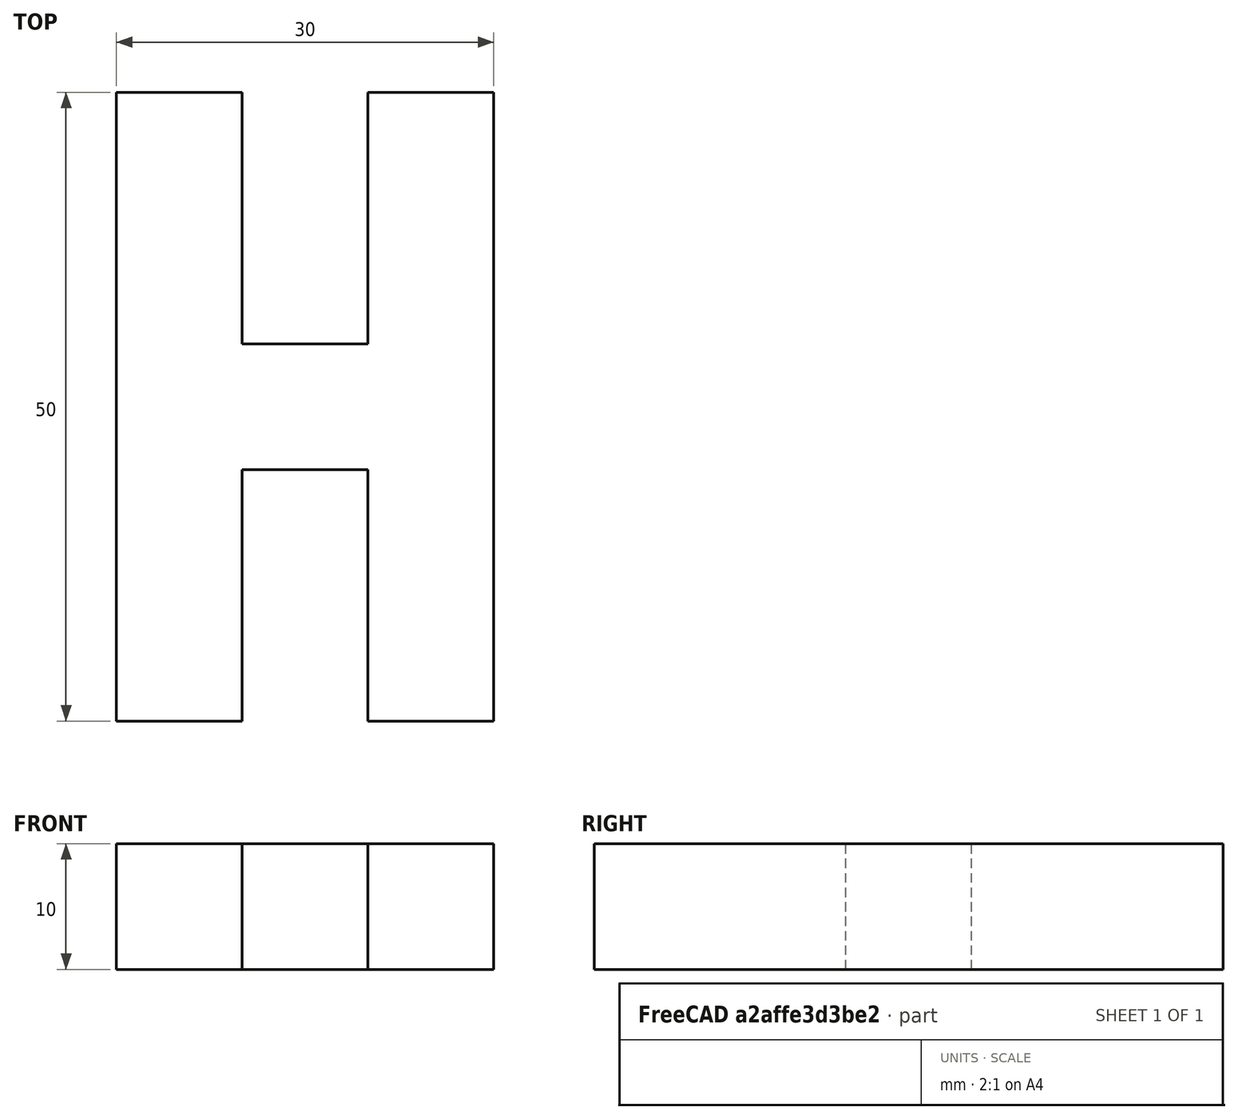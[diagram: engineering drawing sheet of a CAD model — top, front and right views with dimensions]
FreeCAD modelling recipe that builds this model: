
FCSTD DOCUMENT  (FreeCAD 0.21R33694 (Git))
Label: OJT1_T18R02_hola
License: All rights reserved
LicenseURL: https://en.wikipedia.org/wiki/All_rights_reserved
objects: Sketcher::SketchObject×2, PartDesign::Pad×1, PartDesign::Body×1
note: 5 computed .brp shape members not serialized (recipe doc carries the construction recipe); baked Part::Feature solids carry a one-line shape summary decoded from their .brp

FEATURE [Sketcher::SketchObject] Sketch
  FullyConstrained = false
  MapMode = 5
  Support = -> [XY_Plane]
  sketch-geometry (12):
    g0: LineSegment StartX=17.5793 StartY=23.0862 StartZ=0 EndX=17.5793 EndY=-26.9138 EndZ=0
    g1: LineSegment StartX=17.5793 StartY=23.0862 StartZ=0 EndX=27.5793 EndY=23.0862 EndZ=0
    g2: LineSegment StartX=27.5793 StartY=23.0862 StartZ=0 EndX=27.5793 EndY=3.08618 EndZ=0
    g3: LineSegment StartX=27.5793 StartY=3.08618 StartZ=0 EndX=37.5793 EndY=3.08618 EndZ=0
    g4: LineSegment StartX=37.5793 StartY=23.0862 StartZ=0 EndX=37.5793 EndY=3.08618 EndZ=0
    g5: LineSegment StartX=37.5793 StartY=23.0862 StartZ=0 EndX=47.5793 EndY=23.0862 EndZ=0
    g6: LineSegment StartX=47.5793 StartY=23.0862 StartZ=0 EndX=47.5793 EndY=-26.9138 EndZ=0
    g7: LineSegment StartX=37.5793 StartY=-6.91382 StartZ=0 EndX=37.5793 EndY=-26.9138 EndZ=0
    g8: LineSegment StartX=37.5793 StartY=-26.9138 StartZ=0 EndX=47.5793 EndY=-26.9138 EndZ=0
    g9: LineSegment StartX=37.5793 StartY=-6.91382 StartZ=0 EndX=27.5793 EndY=-6.91382 EndZ=0
    g10: LineSegment StartX=27.5793 StartY=-6.91382 StartZ=0 EndX=27.5793 EndY=-26.9138 EndZ=0
    g11: LineSegment StartX=17.5793 StartY=-26.9138 StartZ=0 EndX=27.5793 EndY=-26.9138 EndZ=0
  constraints (34):
    c: Vertical(g0)
    c: Vertical(g2)
    c: Vertical(g4)
    c: Horizontal(g5)
    c: Vertical(g7)
    c: Horizontal(g8)
    c: Horizontal(g9)
    c: Vertical(g10)
    c: Horizontal(g11)
    c: Vertical(g6)
    c: Horizontal(g1)
    c: Horizontal(g3)
    c: Coincident(g1,g2)
    c: Coincident(g1,g0)
    c: Coincident(g4,g5)
    c: Coincident(g6,g5)
    c: Coincident(g3,g4)
    c: Coincident(g3,g2)
    c: Coincident(g9,g10)
    c: Coincident(g9,g7)
    c: Coincident(g8,g7)
    c: Coincident(g8,g6)
    c: Coincident(g10,g11)
    c: Coincident(g0,g11)
    c: DistanceY(g0,g0) = 50
    c: Equal(g6,g0)
    c: DistanceX(g2,g3) = 10
    c: Equal(g3,g9)
    c: DistanceY(g10,g9) = 20
    c: Equal(g10,g7)
    c: DistanceX(g0,g1) = 10
    c: Equal(g1,g11)
    c: DistanceX(g5,g5) = 10
    c: DistanceY(g3,g4) = 20
FEATURE [PartDesign::Pad] Pad
  Direction = (0,0,1)
  Length = 10
  Length2 = 10
  Profile = -> Sketch
  ReferenceAxis = -> Sketch [N_Axis]
  Type = 0
FEATURE [Sketcher::SketchObject] Sketch001
  FullyConstrained = false
  MapMode = 5
  Support = -> [XY_Plane]
  sketch-geometry (4):
    g0: LineSegment StartX=59.5741 StartY=21.7879 StartZ=0 EndX=59.5741 EndY=-25.8817 EndZ=0
    g1: LineSegment StartX=59.5741 StartY=-25.8817 StartZ=0 EndX=83.138 EndY=-25.8817 EndZ=0
    g2: LineSegment StartX=83.138 StartY=21.7879 StartZ=0 EndX=83.138 EndY=-25.8817 EndZ=0
    g3: LineSegment StartX=59.5741 StartY=21.7879 StartZ=0 EndX=83.138 EndY=21.7879 EndZ=0
  constraints (8):
    c: Vertical(g0)
    c: Horizontal(g1)
    c: Horizontal(g3)
    c: Vertical(g2)
    c: Coincident(g3,g0)
    c: Coincident(g3,g2)
    c: Coincident(g1,g2)
    c: Coincident(g1,g0)
FEATURE [PartDesign::Body] Body
  Group = -> [Sketch,Pad,Sketch001]
  Origin = -> Origin
  Tip = -> Pad
